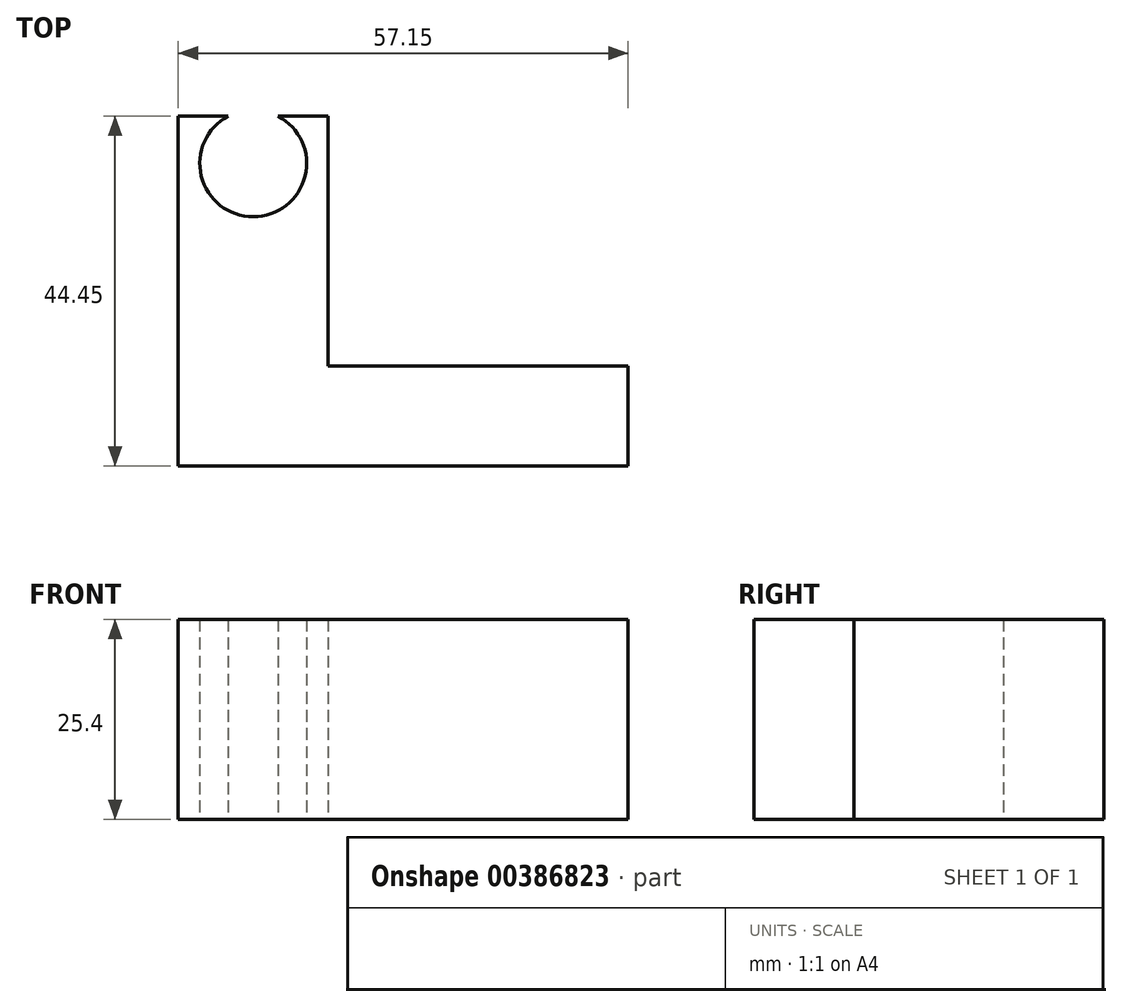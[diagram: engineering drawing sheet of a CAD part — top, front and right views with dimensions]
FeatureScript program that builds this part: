
annotation { "Feature Type Name" : "Feature", "Feature Type Description" : "" }
export const myFeature = defineFeature(function(context is Context, id is Id, definition is map)
    precondition{}
    {
        {
            var Q0;
            Q0=qCreatedBy(makeId("Top.planeOp"),FACE);
            var sketch = newSketch(context, id + "F0", { "sketchPlane" : qUnion([Q0])});
            skLineSegment(sketch, "E0", {"start": v(0, 0) * mm, "end": v(57.15, 0) * mm});
            skLineSegment(sketch, "E1", {"start": v(57.15, 0) * mm, "end": v(57.15, 12.7) * mm});
            skLineSegment(sketch, "E2", {"start": v(0, 0) * mm, "end": v(0, 44.45) * mm});
            skLineSegment(sketch, "E3", {"start": v(0, 44.45) * mm, "end": v(6.35, 44.45) * mm});
            skLineSegment(sketch, "E4", {"start": v(57.15, 12.7) * mm, "end": v(19.05, 12.7) * mm});
            skLineSegment(sketch, "E5", {"start": v(19.05, 12.7) * mm, "end": v(19.05, 44.45) * mm});
            skLineSegment(sketch, "E6", {"start": v(19.05, 44.45) * mm, "end": v(12.7, 44.45) * mm});
            skArc(sketch, "E7", {"start": v(6.35, 44.45) * mm, "mid": v(9.53, 31.66) * mm, "end": v(12.7, 44.45) * mm});
            skSolve(sketch);
        }
        {
            var Q0;
            Q0=makeQuery(id+"F0.imprint","IMPRINT",FACE,{"disambiguationData":[TD([[makeQuery(id+"F0.imprint","IMPRINT",EDGE,{"derivedFrom":sQuery(id+"F0.wireOp",EDGE,"E0")}),1.0]])]});
            extrude(context, id + "F1", {"entities" : qUnion([Q0]), "depth" : 25.4 * mm});
        }
    });
